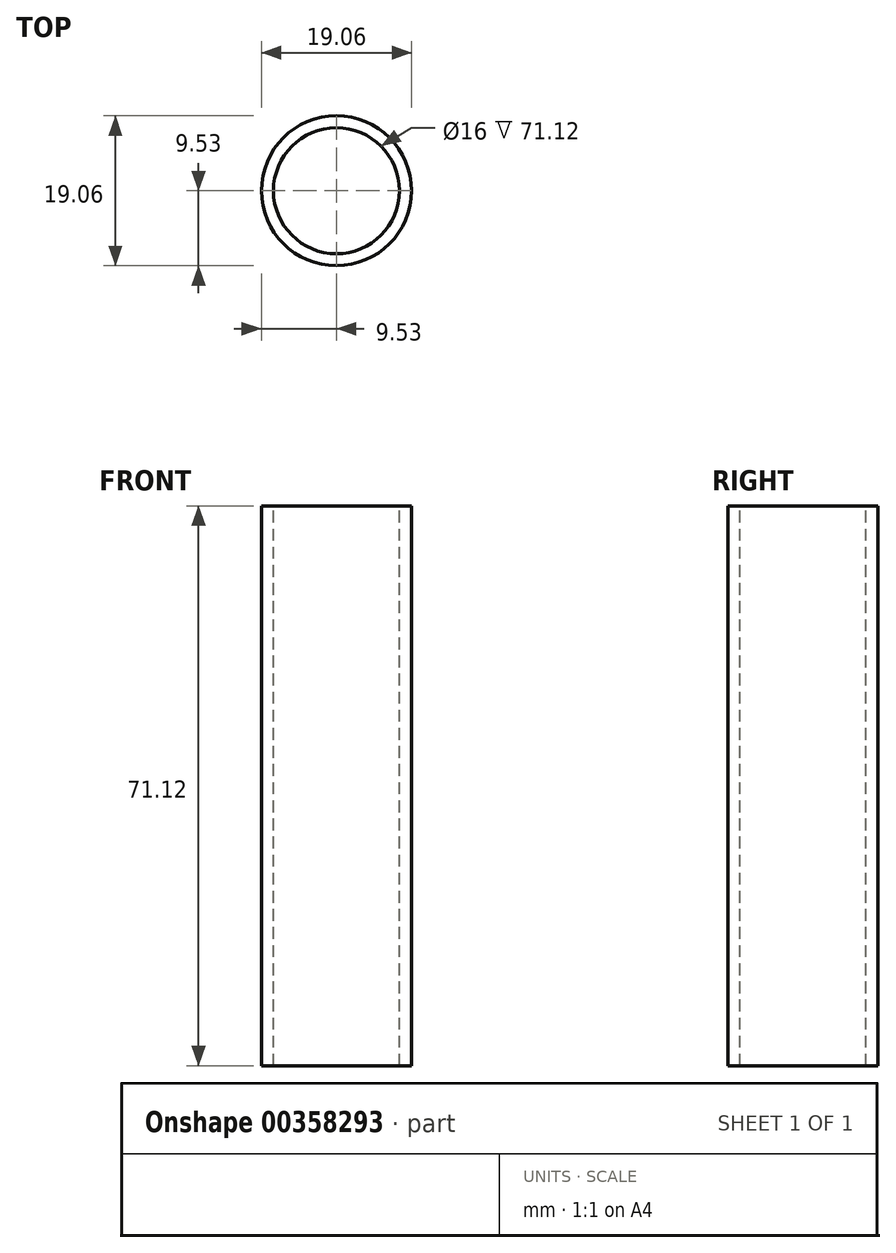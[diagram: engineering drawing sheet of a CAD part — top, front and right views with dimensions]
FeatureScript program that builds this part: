
annotation { "Feature Type Name" : "Feature", "Feature Type Description" : "" }
export const myFeature = defineFeature(function(context is Context, id is Id, definition is map)
    precondition{}
    {
        {
            var Q0;
            Q0=qCreatedBy(makeId("Top.planeOp"),FACE);
            var sketch = newSketch(context, id + "F0", { "sketchPlane" : qUnion([Q0])});
            skCircle(sketch, "E0", {"center": v(0, 0) * mm, "radius": 9.53 * mm});
            skSolve(sketch);
        }
        {
            var Q0;
            Q0 = qSketchRegion(id + "F0", true);
            extrude(context, id + "F1", {"entities" : qUnion([Q0]), "offsetDistance" : 25.4 * mm, "depth" : 71.12 * mm});
        }
        {
            var Q0;
            Q0=makeQuery(id+"F1.opExtrude","CAP_FACE",FACE,{"disambiguationData":[OSD([sQuery(id+"F0.wireOp",EDGE,"E0")])],"isStart":false});
            var sketch = newSketch(context, id + "F2", { "sketchPlane" : qUnion([Q0])});
            skCircle(sketch, "E1", {"center": v(0, 0) * mm, "radius": 8 * mm});
            skSolve(sketch);
        }
        {
            var Q0;
            Q0 = qSketchRegion(id + "F2", true);
            extrude(context, id + "F3", {"entities" : qUnion([Q0]), "operationType" : NewBodyOperationType.REMOVE, "oppositeDirection" : true, "depth" : 72.39 * mm});
        }
    });
